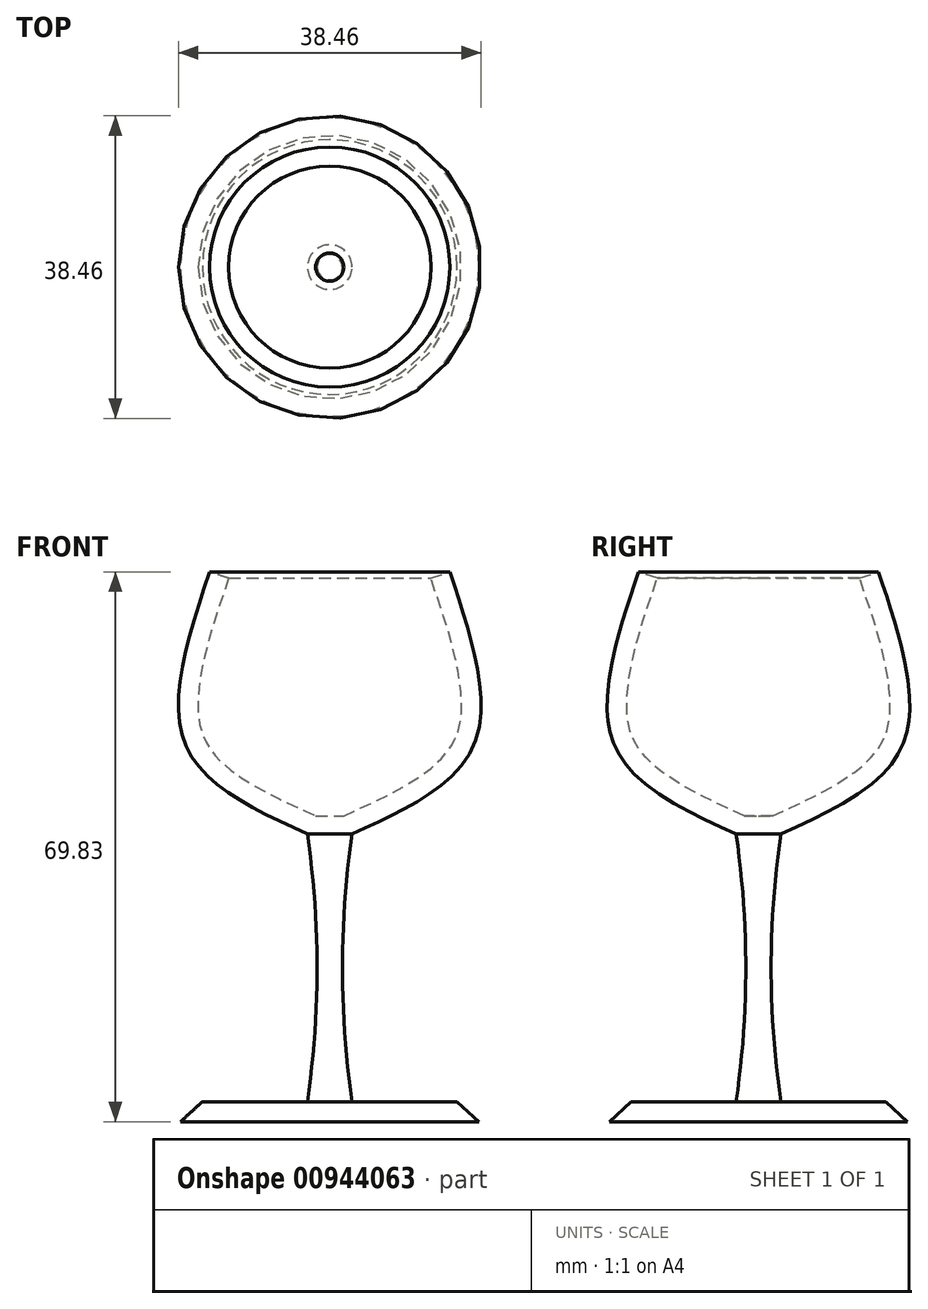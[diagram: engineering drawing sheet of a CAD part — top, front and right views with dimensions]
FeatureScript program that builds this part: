
annotation { "Feature Type Name" : "Feature", "Feature Type Description" : "" }
export const myFeature = defineFeature(function(context is Context, id is Id, definition is map)
    precondition{}
    {
        {
            var Q0;
            Q0=qCreatedBy(makeId("Right.planeOp"),FACE);
            var sketch = newSketch(context, id + "F0", { "sketchPlane" : qUnion([Q0])});
            skFitSpline(sketch, "E0", {"points": [v(15.26, 67.3) * mm, v(18.3, 45.26) * mm, v(2.84, 34.01) * mm], "startDerivative": vector(15.73, -47.4) * mm, "endDerivative": vector(-41.3, -18.79) * mm});
            skFitSpline(sketch, "E1.0", {"points": [v(12.85, 66.5) * mm, v(13.5, 64.52) * mm, v(14.8, 60.6) * mm, v(16.03, 56.03) * mm, v(16.58, 52.7) * mm, v(16.74, 50.42) * mm, v(16.6, 48.4) * mm, v(16.27, 46.97) * mm, v(15.85, 45.96) * mm, v(15.45, 45.23) * mm, v(14.96, 44.51) * mm, v(14.18, 43.58) * mm, v(12.97, 42.44) * mm, v(11.19, 41.13) * mm, v(9.11, 39.87) * mm, v(6.05, 38.27) * mm, v(3.5, 37.1) * mm, v(1.79, 36.33) * mm]});
            skPoint(sketch, "E2.MirrorCS.end.orphan", {"position": v(-2.84, 34.01) * mm});
            skPoint(sketch, "E2.MirrorCS.start.orphan", {"position": v(0, 34.01) * mm});
            skPoint(sketch, "E3.MirrorCS.start.orphan", {"position": v(-15.26, 67.3) * mm});
            skLineSegment(sketch, "E4", {"start": v(12.85, 66.5) * mm, "end": v(15.26, 67.3) * mm});
            skLineSegment(sketch, "E5", {"start": v(1.79, 36.33) * mm, "end": v(0, 36.33) * mm});
            skLineSegment(sketch, "E6", {"start": v(0, 36.33) * mm, "end": v(0, 34.01) * mm});
            skPoint(sketch, "E7.end.orphan", {"position": v(1.79, 34.01) * mm});
            skLineSegment(sketch, "E8", {"start": v(0, 34.01) * mm, "end": v(0, 74.55) * mm});
            skArc(sketch, "E9", {"start": v(2.84, 34.01) * mm, "mid": v(1.61, 17) * mm, "end": v(2.84, 0) * mm});
            skLineSegment(sketch, "E10", {"start": v(0, 34.01) * mm, "end": v(0, 0) * mm});
            skLineSegment(sketch, "E11", {"start": v(0, 0) * mm, "end": v(2.84, 0) * mm});
            skSolve(sketch);
        }
        {
            var Q0;
            Q0=makeQuery(id+"F0.imprint","IMPRINT",FACE,{"disambiguationData":[TD([[makeQuery(id+"F0.imprint","IMPRINT",EDGE,{"derivedFrom":sQuery(id+"F0.wireOp",EDGE,"E0")}),-1.0]])]});
            var Q1;
            Q1=sQuery(id+"F0.wireOp",EDGE,"E8");
            revolve(context, id + "F1", {"surfaceOperationType" : NewSurfaceOperationType.NEW, "entities" : qUnion([Q0]), "axis" : qUnion([Q1]), "revolveType" : RevolveType.FULL});
        }
        {
            var Q0;
            Q0=makeQuery(id+"F1.opRevolve","SWEPT_FACE",FACE,{"disambiguationData":[OSD([sQuery(id+"F0.wireOp",EDGE,"E11")])]});
            var sketch = newSketch(context, id + "F2", { "sketchPlane" : qUnion([Q0])});
            skCircle(sketch, "E12", {"center": v(0, 0) * mm, "radius": 20.83 * mm});
            skSolve(sketch);
        }
        {
            var Q0;
            Q0 = qSketchRegion(id + "F2", true);
            extrude(context, id + "F3", {"entities" : qUnion([Q0]), "operationType" : NewBodyOperationType.ADD, "depth" : 2.54 * mm, "offsetDistance" : 25.4 * mm, "hasDraft" : true, "draftAngle" : 5 * degree});
        }
        {
            var Q0;
            Q0=makeQuery(id+"F3.opExtrude","CAP_EDGE",EDGE,{"disambiguationData":[OSD([sQuery(id+"F2.wireOp",EDGE,"E12")])],"isStart":true});
            chamfer(context, id + "F4", {"entities" : qUnion([Q0]), "width" : 5.08 * mm, "tangentPropagation" : true});
        }
    });
